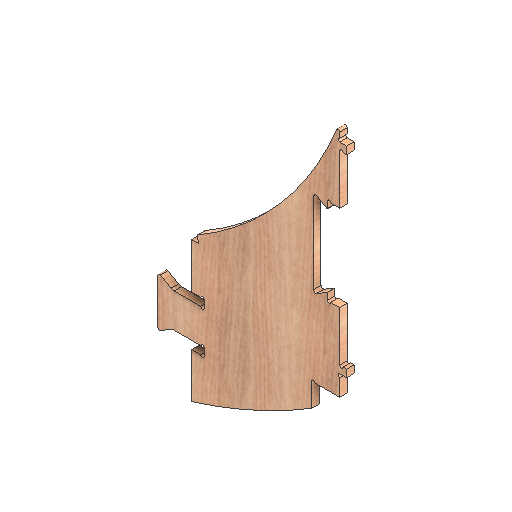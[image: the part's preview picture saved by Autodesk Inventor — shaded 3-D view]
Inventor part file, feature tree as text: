
AUTODESK INVENTOR PART (.ipt)
format: ipt  version: 2021 (Build 250183000, 183)  size: 241,152 bytes
history: native  units: mm
features: other x2, hole x1, extrude x1
ambient origin geometry x8: Origin, YZ Plane, XZ Plane, XY Plane, X Axis, Y Axis, Z Axis, Center Point
bodies: Solid1 (feature_tree)
feature tree (4):
  other  "CONTOURS"
  hole  "HOLES"  [1 undecoded]
  other  "LETTERS"
  extrude  "Extrusion3"  Depth=0.5mm
note: 1 required parameter value undecoded (feature->parameter linkage not recoverable at this tier; creation-order binding heuristic only, values carry confidence <= 0.55)
